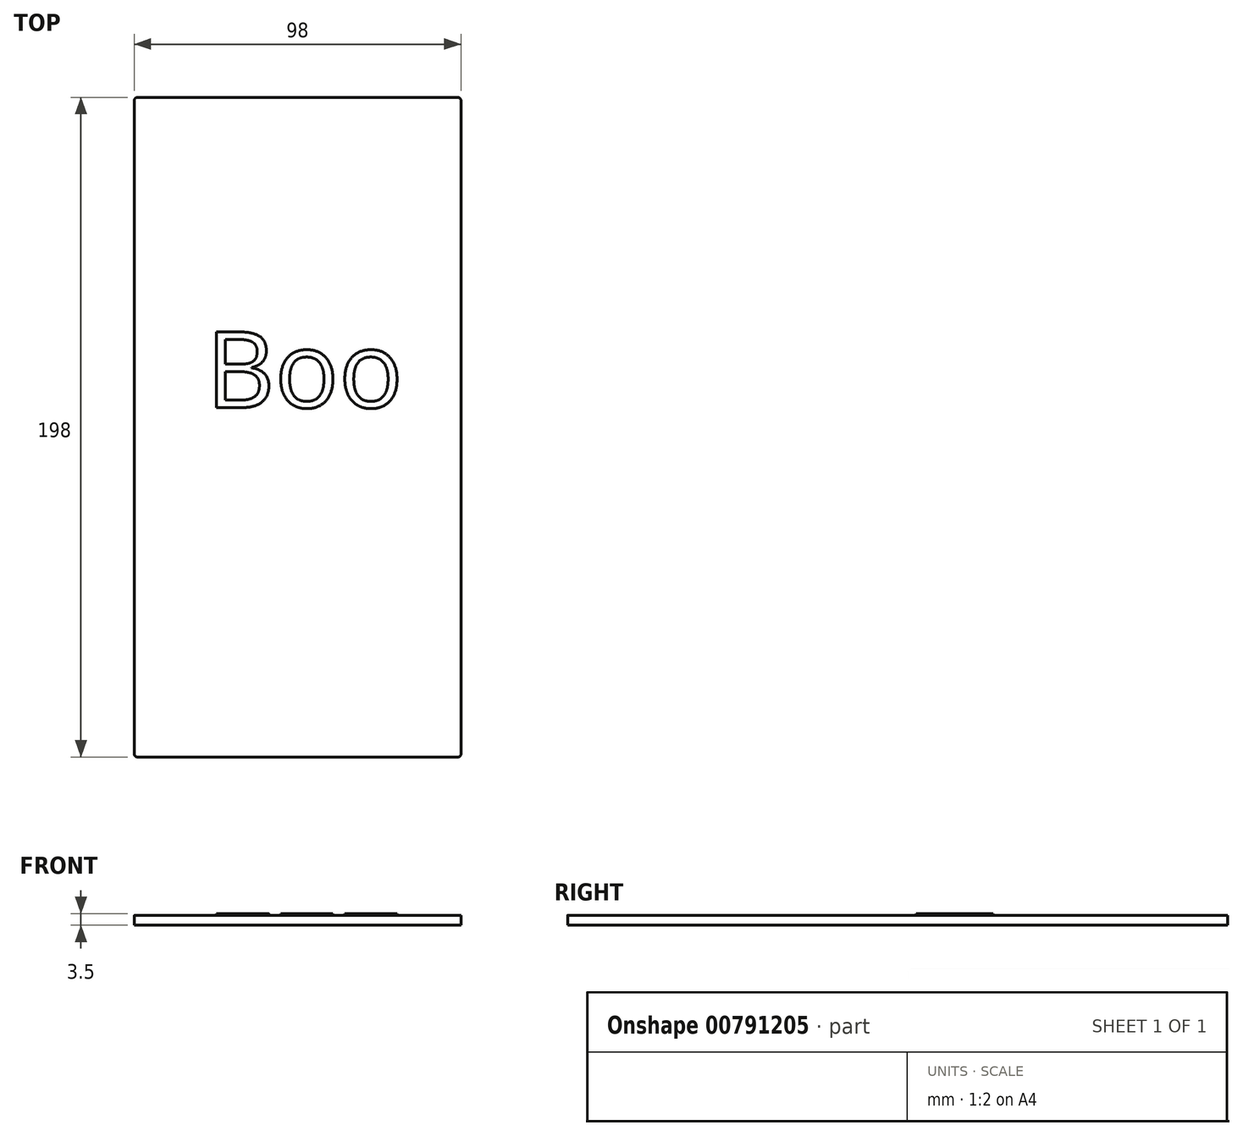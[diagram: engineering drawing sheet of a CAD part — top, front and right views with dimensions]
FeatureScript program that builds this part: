
annotation { "Feature Type Name" : "Feature", "Feature Type Description" : "" }
export const myFeature = defineFeature(function(context is Context, id is Id, definition is map)
    precondition{}
    {
        {
            var Q0;
            Q0=qCreatedBy(makeId("Top.planeOp"),FACE);
            var sketch = newSketch(context, id + "F0", { "sketchPlane" : qUnion([Q0])});
            skLineSegment(sketch, "E0.bottom", {"start": v(0, 0) * mm, "end": v(98, 0) * mm});
            skLineSegment(sketch, "E0.top", {"start": v(0, 198) * mm, "end": v(98, 198) * mm});
            skLineSegment(sketch, "E0.left", {"start": v(0, 0) * mm, "end": v(0, 198) * mm});
            skLineSegment(sketch, "E0.right", {"start": v(98, 0) * mm, "end": v(98, 198) * mm});
            skSolve(sketch);
        }
        {
            var Q0;
            Q0=makeQuery(id+"F0.imprint","IMPRINT",FACE,{"disambiguationData":[TD([[makeQuery(id+"F0.imprint","IMPRINT",EDGE,{"derivedFrom":sQuery(id+"F0.wireOp",EDGE,"E0.bottom")}),1.0]])]});
            extrude(context, id + "F1", {"entities" : qUnion([Q0]), "depth" : 3 * mm, "offsetDistance" : 25 * mm});
        }
        {
            var Q0;
            Q0=makeQuery(id+"F1.opExtrude","SWEPT_EDGE",EDGE,{"disambiguationData":[OSD([sQuery(id+"F0.wireOp",EDGE,"E0.bottom"),sQuery(id+"F0.wireOp",EDGE,"E0.left")])]});
            var Q1;
            Q1=makeQuery(id+"F1.opExtrude","SWEPT_EDGE",EDGE,{"disambiguationData":[OSD([sQuery(id+"F0.wireOp",EDGE,"E0.bottom"),sQuery(id+"F0.wireOp",EDGE,"E0.right")])]});
            fillet(context, id + "F2", {"entities" : qUnion([Q0, Q1]), "radius" : 0.9 * mm, "tangentPropagation" : true, "allowEdgeOverflow" : false});
        }
        {
            var Q0;
            Q0=makeQuery(id+"F1.opExtrude","SWEPT_EDGE",EDGE,{"disambiguationData":[OSD([sQuery(id+"F0.wireOp",EDGE,"E0.top"),sQuery(id+"F0.wireOp",EDGE,"E0.left")])]});
            var Q1;
            Q1=makeQuery(id+"F1.opExtrude","SWEPT_EDGE",EDGE,{"disambiguationData":[OSD([sQuery(id+"F0.wireOp",EDGE,"E0.top"),sQuery(id+"F0.wireOp",EDGE,"E0.right")])]});
            fillet(context, id + "F3", {"entities" : qUnion([Q0, Q1]), "radius" : 1 * mm, "tangentPropagation" : true, "allowEdgeOverflow" : false});
        }
        {
            var Q0;
            Q0=makeQuery(id+"F1.opExtrude","CAP_FACE",FACE,{"disambiguationData":[OSD([sQuery(id+"F0.wireOp",EDGE,"E0.bottom"),sQuery(id+"F0.wireOp",EDGE,"E0.top"),sQuery(id+"F0.wireOp",EDGE,"E0.left"),sQuery(id+"F0.wireOp",EDGE,"E0.right")])],"isStart":false});
            var sketch = newSketch(context, id + "F4", { "sketchPlane" : qUnion([Q0])});
            skText(sketch, "E1", { "text": "Boo!", "fontName": "OpenSans-Regular.ttf"});
            const initialGuessF4  = {"E1": [0.01308, 0.10313, 1, 0, 0.02357]};
            skSetInitialGuess(sketch, initialGuessF4);
            skSolve(sketch);
        }
        {
            var Q0;
            Q0 = qSketchRegion(id + "F4", true);
            extrude(context, id + "F5", {"entities" : qUnion([Q0]), "operationType" : NewBodyOperationType.ADD, "oppositeDirection" : true, "depth" : 1 * mm, "offsetDistance" : 25 * mm});
        }
        {
            var Q0;
            Q0=qCreatedBy(makeId("Top.planeOp"),FACE);
            var sketch = newSketch(context, id + "F6", { "sketchPlane" : qUnion([Q0])});
            skText(sketch, "E2", { "text": "Boo", "fontName": "OpenSans-Regular.ttf"});
            const initialGuessF6  = {"E2": [0.02148, 0.10488, 1, 0, 0.02294]};
            skSetInitialGuess(sketch, initialGuessF6);
            skSolve(sketch);
        }
        {
            var Q0;
            Q0 = qSketchRegion(id + "F6", true);
            extrude(context, id + "F7", {"entities" : qUnion([Q0]), "operationType" : NewBodyOperationType.ADD, "depth" : 3.5 * mm, "offsetDistance" : 25 * mm});
        }
    });
